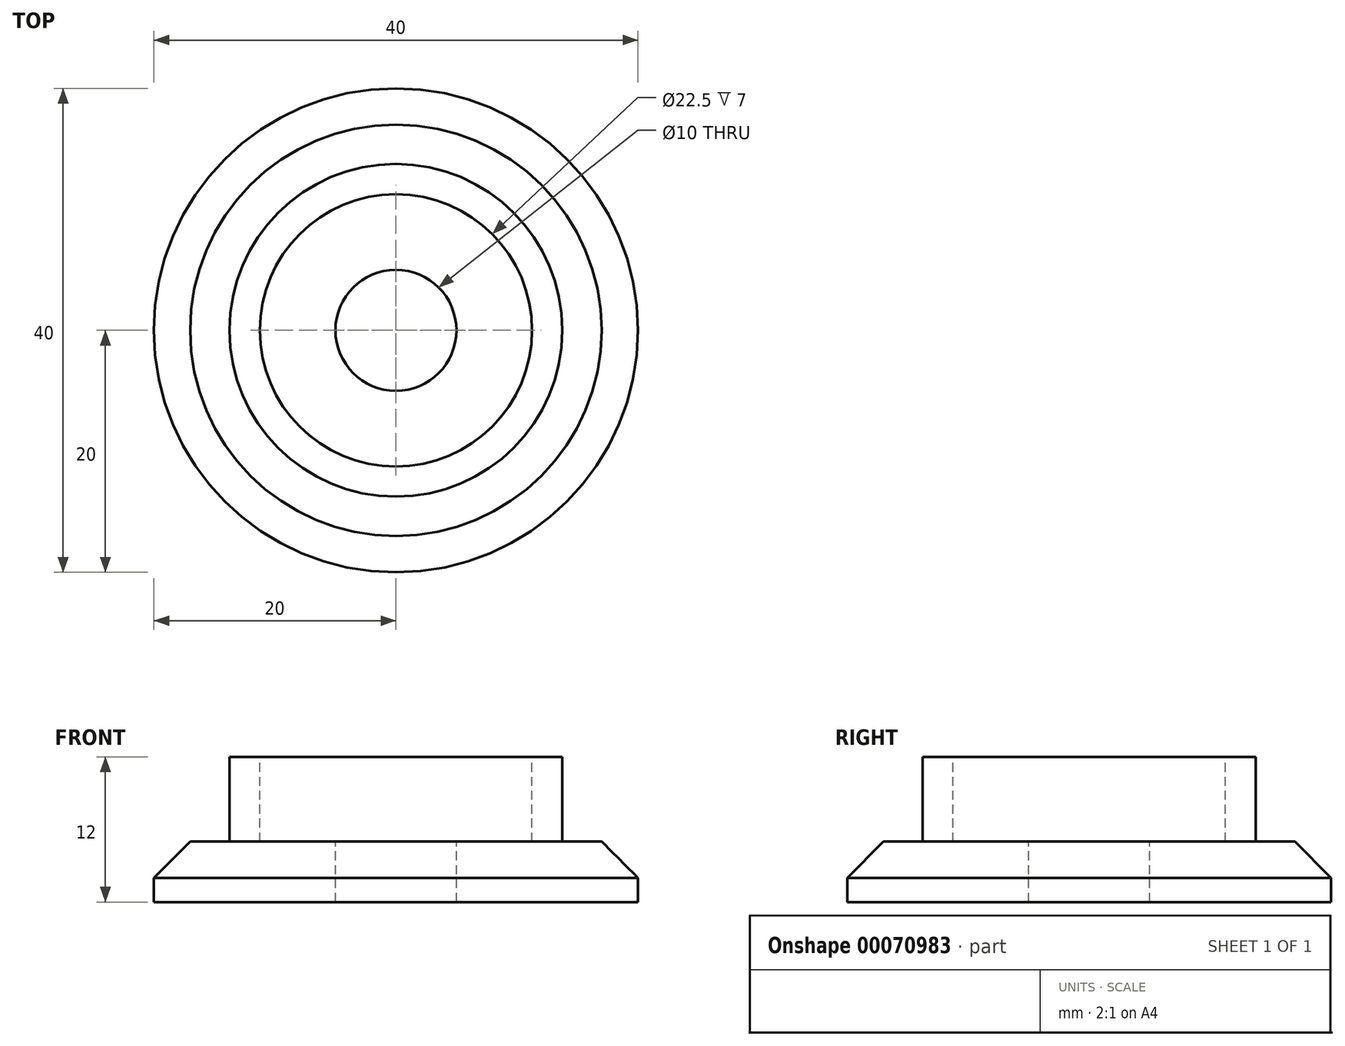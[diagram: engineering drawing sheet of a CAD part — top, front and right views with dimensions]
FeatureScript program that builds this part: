
annotation { "Feature Type Name" : "Feature", "Feature Type Description" : "" }
export const myFeature = defineFeature(function(context is Context, id is Id, definition is map)
    precondition{}
    {
        {
            var Q0;
            Q0=qCreatedBy(makeId("Top.planeOp"),FACE);
            var sketch = newSketch(context, id + "F0", { "sketchPlane" : qUnion([Q0])});
            skCircle(sketch, "E0", {"center": v(0, 0) * mm, "radius": 20 * mm});
            skSolve(sketch);
        }
        {
            var Q0;
            Q0 = qSketchRegion(id + "F0", true);
            extrude(context, id + "F1", {"entities" : qUnion([Q0]), "depth" : 5 * mm});
        }
        {
            var Q0;
            Q0=makeQuery(id+"F1.opExtrude","CAP_FACE",FACE,{"disambiguationData":[OSD([sQuery(id+"F0.wireOp",EDGE,"E0")])],"isStart":false});
            var sketch = newSketch(context, id + "F2", { "sketchPlane" : qUnion([Q0])});
            skCircle(sketch, "E1", {"center": v(0, 0) * mm, "radius": 13.75 * mm});
            skSolve(sketch);
        }
        {
            var Q0;
            Q0 = qSketchRegion(id + "F2", true);
            extrude(context, id + "F3", {"entities" : qUnion([Q0]), "operationType" : NewBodyOperationType.ADD, "depth" : 7 * mm});
        }
        {
            var Q0;
            Q0=makeQuery(id+"F3.opExtrude","CAP_FACE",FACE,{"disambiguationData":[OSD([sQuery(id+"F2.wireOp",EDGE,"E1")])],"isStart":false});
            var sketch = newSketch(context, id + "F4", { "sketchPlane" : qUnion([Q0])});
            skCircle(sketch, "E2", {"center": v(0, 0) * mm, "radius": 11.25 * mm});
            skSolve(sketch);
        }
        {
            var Q0;
            Q0=makeQuery(id+"F1.opExtrude","CAP_EDGE",EDGE,{"disambiguationData":[OSD([sQuery(id+"F0.wireOp",EDGE,"E0")])],"isStart":false});
            chamfer(context, id + "F5", {"entities" : qUnion([Q0]), "width" : 3 * mm, "tangentPropagation" : true});
        }
        {
            var Q0;
            Q0 = qSketchRegion(id + "F4", true);
            extrude(context, id + "F6", {"entities" : qUnion([Q0]), "operationType" : NewBodyOperationType.REMOVE, "oppositeDirection" : true, "depth" : 7 * mm});
        }
        {
            var Q0;
            Q0=makeQuery(id+"F6.boolean.opBoolean","COPY",FACE,{"derivedFrom":makeQuery(id+"F6.opExtrude","CAP_FACE",FACE,{"disambiguationData":[OSD([sQuery(id+"F4.wireOp",EDGE,"E2")])],"isStart":false})});
            var sketch = newSketch(context, id + "F7", { "sketchPlane" : qUnion([Q0])});
            skCircle(sketch, "E3", {"center": v(0, 0) * mm, "radius": 5 * mm});
            skSolve(sketch);
        }
        {
            var Q0;
            Q0 = qSketchRegion(id + "F7", true);
            var Q1;
            Q1=makeQuery(id+"F1.opExtrude","CAP_FACE",FACE,{"disambiguationData":[OSD([sQuery(id+"F0.wireOp",EDGE,"E0")])],"isStart":true});
            extrude(context, id + "F8", {"entities" : qUnion([Q0]), "operationType" : NewBodyOperationType.REMOVE, "endBound" : BoundingType.UP_TO_SURFACE, "oppositeDirection" : true, "endBoundEntityFace" : qUnion([Q1]), "depth" : 25 * mm});
        }
    });
